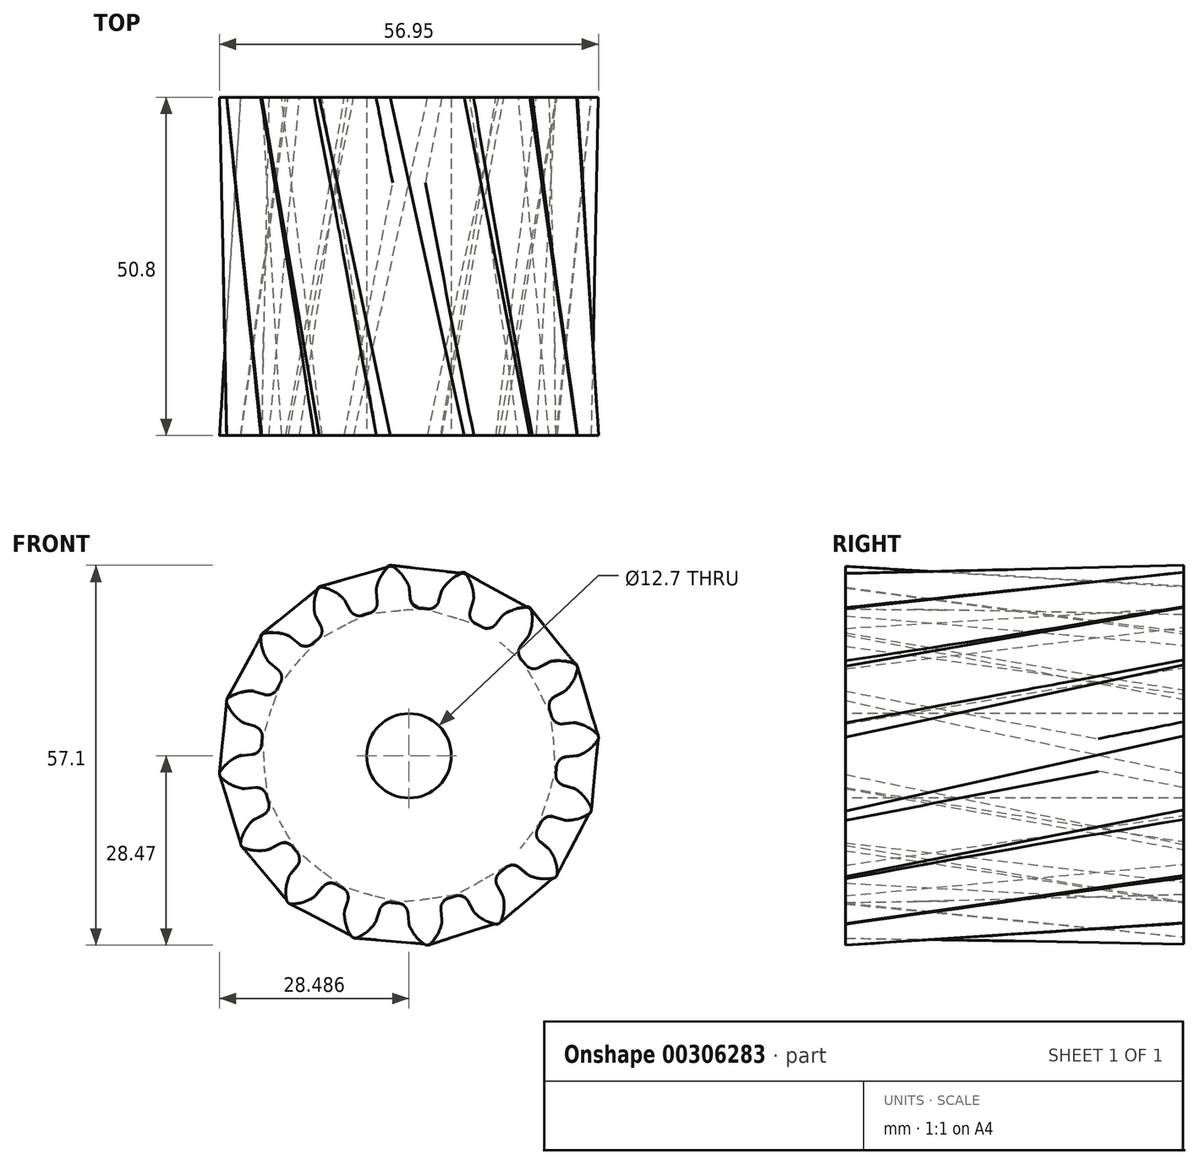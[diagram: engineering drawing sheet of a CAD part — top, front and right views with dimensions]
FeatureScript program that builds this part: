
annotation { "Feature Type Name" : "Feature", "Feature Type Description" : "" }
export const myFeature = defineFeature(function(context is Context, id is Id, definition is map)
    precondition{}
    {
        {
            var Q0;
            Q0=qCreatedBy(makeId("Front.planeOp"),FACE);
            var sketch = newSketch(context, id + "F0", { "sketchPlane" : qUnion([Q0])});
            skArc(sketch, "E0", {"start": v(-5.93, 21.42) * mm, "mid": v(-6.45, 21.27) * mm, "end": v(-6.97, 21.1) * mm});
            skArc(sketch, "E1.trimOffspring", {"start": v(-0.1, 25.65) * mm, "mid": v(-1.04, 27.17) * mm, "end": v(-2.37, 28.38) * mm});
            skLineSegment(sketch, "E2", {"start": v(0.02, 25.17) * mm, "end": v(0.18, 23.6) * mm});
            skLineSegment(sketch, "E3", {"start": v(-2.65, 28.47) * mm, "end": v(-2.8, 28.47) * mm});
            skLineSegment(sketch, "E4.MirrorCS", {"start": v(-2.95, 28.44) * mm, "end": v(-2.8, 28.47) * mm});
            skArc(sketch, "E5.MirrorCS", {"start": v(-4.9, 25.17) * mm, "mid": v(-4.28, 26.85) * mm, "end": v(-3.22, 28.3) * mm});
            skLineSegment(sketch, "E6.MirrorCS", {"start": v(-4.93, 24.68) * mm, "end": v(-4.78, 23.1) * mm});
            skPoint(sketch, "E7.visualSharp", {"position": v(0.31, 22.22) * mm});
            skArc(sketch, "E7.filletArc", {"start": v(0.18, 23.6) * mm, "mid": v(0.65, 22.61) * mm, "end": v(1.64, 22.16) * mm});
            skPoint(sketch, "E8.visualSharp", {"position": v(-4.64, 21.73) * mm});
            skArc(sketch, "E8.filletArc", {"start": v(-5.93, 21.42) * mm, "mid": v(-5.05, 22.05) * mm, "end": v(-4.78, 23.1) * mm});
            skPoint(sketch, "E9.visualSharp", {"position": v(-4.96, 24.91) * mm});
            skArc(sketch, "E9.filletArc", {"start": v(-4.9, 25.17) * mm, "mid": v(-4.94, 24.93) * mm, "end": v(-4.93, 24.68) * mm});
            skPoint(sketch, "E10.visualSharp", {"position": v(0, 25.4) * mm});
            skArc(sketch, "E10.filletArc", {"start": v(0.02, 25.17) * mm, "mid": v(-0.02, 25.41) * mm, "end": v(-0.1, 25.65) * mm});
            skPoint(sketch, "E11.visualSharp", {"position": v(-3.1, 28.4) * mm});
            skArc(sketch, "E11.filletArc", {"start": v(-2.95, 28.44) * mm, "mid": v(-3.1, 28.38) * mm, "end": v(-3.22, 28.3) * mm});
            skPoint(sketch, "E12.visualSharp", {"position": v(-2.5, 28.47) * mm});
            skArc(sketch, "E12.filletArc", {"start": v(-2.37, 28.38) * mm, "mid": v(-2.5, 28.44) * mm, "end": v(-2.65, 28.47) * mm});
            skArc(sketch, "E13.1.0", {"start": v(-13.68, 17.52) * mm, "mid": v(-13.1, 18.44) * mm, "end": v(-13.26, 19.52) * mm});
            skPoint(sketch, "E13.1.1", {"position": v(-14.11, 21.12) * mm});
            skLineSegment(sketch, "E13.1.2", {"start": v(-9.61, 23.26) * mm, "end": v(-8.86, 21.86) * mm});
            skPoint(sketch, "E13.1.3", {"position": v(-9.72, 23.47) * mm});
            skArc(sketch, "E13.1.4", {"start": v(-14.16, 21.38) * mm, "mid": v(-14.23, 23.17) * mm, "end": v(-13.8, 24.9) * mm});
            skLineSegment(sketch, "E13.1.5", {"start": v(-14, 20.92) * mm, "end": v(-13.26, 19.52) * mm});
            skArc(sketch, "E13.1.6", {"start": v(-8.86, 21.86) * mm, "mid": v(-8.05, 21.14) * mm, "end": v(-6.97, 21.1) * mm});
            skArc(sketch, "E13.1.7", {"start": v(-9.9, 23.66) * mm, "mid": v(-11.36, 24.7) * mm, "end": v(-13.05, 25.31) * mm});
            skPoint(sketch, "E13.1.8", {"position": v(-13.74, 25.06) * mm});
            skPoint(sketch, "E13.1.9", {"position": v(-13.2, 25.34) * mm});
            skArc(sketch, "E13.1.10", {"start": v(-14.16, 21.38) * mm, "mid": v(-14.1, 21.14) * mm, "end": v(-14, 20.92) * mm});
            skArc(sketch, "E13.1.11", {"start": v(-9.61, 23.26) * mm, "mid": v(-9.74, 23.47) * mm, "end": v(-9.9, 23.66) * mm});
            skLineSegment(sketch, "E13.1.12", {"start": v(-13.34, 25.28) * mm, "end": v(-13.48, 25.23) * mm});
            skLineSegment(sketch, "E13.1.13", {"start": v(-13.61, 25.14) * mm, "end": v(-13.48, 25.23) * mm});
            skArc(sketch, "E13.1.14", {"start": v(-13.61, 25.14) * mm, "mid": v(-13.72, 25.04) * mm, "end": v(-13.8, 24.9) * mm});
            skArc(sketch, "E13.1.15", {"start": v(-13.05, 25.31) * mm, "mid": v(-13.2, 25.32) * mm, "end": v(-13.34, 25.28) * mm});
            skArc(sketch, "E13.2.0", {"start": v(-19.34, 10.95) * mm, "mid": v(-19.16, 12.02) * mm, "end": v(-19.71, 12.96) * mm});
            skPoint(sketch, "E13.2.1", {"position": v(-21.12, 14.11) * mm});
            skLineSegment(sketch, "E13.2.2", {"start": v(-17.78, 17.81) * mm, "end": v(-16.56, 16.8) * mm});
            skPoint(sketch, "E13.2.3", {"position": v(-17.96, 17.96) * mm});
            skArc(sketch, "E13.2.4", {"start": v(-21.27, 14.33) * mm, "mid": v(-22.02, 15.96) * mm, "end": v(-22.28, 17.73) * mm});
            skLineSegment(sketch, "E13.2.5", {"start": v(-20.94, 13.97) * mm, "end": v(-19.71, 12.96) * mm});
            skArc(sketch, "E13.2.6", {"start": v(-16.56, 16.8) * mm, "mid": v(-15.53, 16.45) * mm, "end": v(-14.51, 16.83) * mm});
            skArc(sketch, "E13.2.7", {"start": v(-18.2, 18.06) * mm, "mid": v(-19.95, 18.48) * mm, "end": v(-21.74, 18.4) * mm});
            skPoint(sketch, "E13.2.8", {"position": v(-22.28, 17.9) * mm});
            skPoint(sketch, "E13.2.9", {"position": v(-21.9, 18.36) * mm});
            skArc(sketch, "E13.2.10", {"start": v(-21.27, 14.33) * mm, "mid": v(-21.12, 14.14) * mm, "end": v(-20.94, 13.97) * mm});
            skArc(sketch, "E13.2.11", {"start": v(-17.78, 17.81) * mm, "mid": v(-17.98, 17.96) * mm, "end": v(-18.2, 18.06) * mm});
            skLineSegment(sketch, "E13.2.12", {"start": v(-22, 18.25) * mm, "end": v(-22.11, 18.15) * mm});
            skLineSegment(sketch, "E13.2.13", {"start": v(-22.2, 18.02) * mm, "end": v(-22.11, 18.15) * mm});
            skArc(sketch, "E13.2.14", {"start": v(-22.2, 18.02) * mm, "mid": v(-22.26, 17.88) * mm, "end": v(-22.28, 17.73) * mm});
            skArc(sketch, "E13.2.15", {"start": v(-21.74, 18.4) * mm, "mid": v(-21.88, 18.34) * mm, "end": v(-22, 18.25) * mm});
            skArc(sketch, "E13.3.0", {"start": v(-22.06, 2.71) * mm, "mid": v(-22.3, 3.77) * mm, "end": v(-23.17, 4.43) * mm});
            skPoint(sketch, "E13.3.1", {"position": v(-24.91, 4.96) * mm});
            skLineSegment(sketch, "E13.3.2", {"start": v(-23.25, 9.65) * mm, "end": v(-21.73, 9.2) * mm});
            skPoint(sketch, "E13.3.3", {"position": v(-23.47, 9.72) * mm});
            skArc(sketch, "E13.3.4", {"start": v(-25.13, 5.1) * mm, "mid": v(-26.45, 6.32) * mm, "end": v(-27.37, 7.86) * mm});
            skLineSegment(sketch, "E13.3.5", {"start": v(-24.7, 4.89) * mm, "end": v(-23.17, 4.43) * mm});
            skArc(sketch, "E13.3.6", {"start": v(-21.73, 9.2) * mm, "mid": v(-20.64, 9.25) * mm, "end": v(-19.85, 10) * mm});
            skArc(sketch, "E13.3.7", {"start": v(-23.73, 9.72) * mm, "mid": v(-25.5, 9.44) * mm, "end": v(-27.12, 8.67) * mm});
            skPoint(sketch, "E13.3.8", {"position": v(-27.43, 8) * mm});
            skPoint(sketch, "E13.3.9", {"position": v(-27.25, 8.59) * mm});
            skArc(sketch, "E13.3.10", {"start": v(-25.13, 5.1) * mm, "mid": v(-24.92, 4.98) * mm, "end": v(-24.7, 4.89) * mm});
            skArc(sketch, "E13.3.11", {"start": v(-23.25, 9.65) * mm, "mid": v(-23.49, 9.7) * mm, "end": v(-23.73, 9.72) * mm});
            skLineSegment(sketch, "E13.3.12", {"start": v(-27.31, 8.44) * mm, "end": v(-27.37, 8.3) * mm});
            skLineSegment(sketch, "E13.3.13", {"start": v(-27.4, 8.15) * mm, "end": v(-27.37, 8.3) * mm});
            skArc(sketch, "E13.3.14", {"start": v(-27.4, 8.15) * mm, "mid": v(-27.4, 8) * mm, "end": v(-27.37, 7.86) * mm});
            skArc(sketch, "E13.3.15", {"start": v(-27.12, 8.67) * mm, "mid": v(-27.24, 8.57) * mm, "end": v(-27.31, 8.44) * mm});
            skArc(sketch, "E13.4.0", {"start": v(-21.42, -5.93) * mm, "mid": v(-22.05, -5.05) * mm, "end": v(-23.1, -4.78) * mm});
            skPoint(sketch, "E13.4.1", {"position": v(-24.91, -4.96) * mm});
            skLineSegment(sketch, "E13.4.2", {"start": v(-25.17, 0.02) * mm, "end": v(-23.6, 0.18) * mm});
            skPoint(sketch, "E13.4.3", {"position": v(-25.4, 0) * mm});
            skArc(sketch, "E13.4.4", {"start": v(-25.17, -4.9) * mm, "mid": v(-26.85, -4.28) * mm, "end": v(-28.3, -3.22) * mm});
            skLineSegment(sketch, "E13.4.5", {"start": v(-24.68, -4.93) * mm, "end": v(-23.1, -4.78) * mm});
            skArc(sketch, "E13.4.6", {"start": v(-23.6, 0.18) * mm, "mid": v(-22.61, 0.65) * mm, "end": v(-22.16, 1.64) * mm});
            skArc(sketch, "E13.4.7", {"start": v(-25.65, -0.1) * mm, "mid": v(-27.17, -1.04) * mm, "end": v(-28.38, -2.37) * mm});
            skPoint(sketch, "E13.4.8", {"position": v(-28.4, -3.1) * mm});
            skPoint(sketch, "E13.4.9", {"position": v(-28.47, -2.5) * mm});
            skArc(sketch, "E13.4.10", {"start": v(-25.17, -4.9) * mm, "mid": v(-24.93, -4.94) * mm, "end": v(-24.68, -4.93) * mm});
            skArc(sketch, "E13.4.11", {"start": v(-25.17, 0.02) * mm, "mid": v(-25.41, -0.02) * mm, "end": v(-25.65, -0.1) * mm});
            skLineSegment(sketch, "E13.4.12", {"start": v(-28.47, -2.65) * mm, "end": v(-28.47, -2.8) * mm});
            skLineSegment(sketch, "E13.4.13", {"start": v(-28.44, -2.95) * mm, "end": v(-28.47, -2.8) * mm});
            skArc(sketch, "E13.4.14", {"start": v(-28.44, -2.95) * mm, "mid": v(-28.38, -3.1) * mm, "end": v(-28.3, -3.22) * mm});
            skArc(sketch, "E13.4.15", {"start": v(-28.38, -2.37) * mm, "mid": v(-28.44, -2.5) * mm, "end": v(-28.47, -2.65) * mm});
            skArc(sketch, "E13.5.0", {"start": v(-17.52, -13.68) * mm, "mid": v(-18.44, -13.1) * mm, "end": v(-19.52, -13.26) * mm});
            skPoint(sketch, "E13.5.1", {"position": v(-21.12, -14.11) * mm});
            skLineSegment(sketch, "E13.5.2", {"start": v(-23.26, -9.61) * mm, "end": v(-21.86, -8.86) * mm});
            skPoint(sketch, "E13.5.3", {"position": v(-23.47, -9.72) * mm});
            skArc(sketch, "E13.5.4", {"start": v(-21.38, -14.16) * mm, "mid": v(-23.17, -14.23) * mm, "end": v(-24.9, -13.8) * mm});
            skLineSegment(sketch, "E13.5.5", {"start": v(-20.92, -14) * mm, "end": v(-19.52, -13.26) * mm});
            skArc(sketch, "E13.5.6", {"start": v(-21.86, -8.86) * mm, "mid": v(-21.14, -8.05) * mm, "end": v(-21.1, -6.97) * mm});
            skArc(sketch, "E13.5.7", {"start": v(-23.66, -9.9) * mm, "mid": v(-24.7, -11.36) * mm, "end": v(-25.31, -13.05) * mm});
            skPoint(sketch, "E13.5.8", {"position": v(-25.06, -13.74) * mm});
            skPoint(sketch, "E13.5.9", {"position": v(-25.34, -13.2) * mm});
            skArc(sketch, "E13.5.10", {"start": v(-21.38, -14.16) * mm, "mid": v(-21.14, -14.1) * mm, "end": v(-20.92, -14) * mm});
            skArc(sketch, "E13.5.11", {"start": v(-23.26, -9.61) * mm, "mid": v(-23.47, -9.74) * mm, "end": v(-23.66, -9.9) * mm});
            skLineSegment(sketch, "E13.5.12", {"start": v(-25.28, -13.34) * mm, "end": v(-25.23, -13.48) * mm});
            skLineSegment(sketch, "E13.5.13", {"start": v(-25.14, -13.61) * mm, "end": v(-25.23, -13.48) * mm});
            skArc(sketch, "E13.5.14", {"start": v(-25.14, -13.61) * mm, "mid": v(-25.04, -13.72) * mm, "end": v(-24.9, -13.8) * mm});
            skArc(sketch, "E13.5.15", {"start": v(-25.31, -13.05) * mm, "mid": v(-25.32, -13.2) * mm, "end": v(-25.28, -13.34) * mm});
            skArc(sketch, "E13.6.0", {"start": v(-10.95, -19.34) * mm, "mid": v(-12.02, -19.16) * mm, "end": v(-12.96, -19.71) * mm});
            skPoint(sketch, "E13.6.1", {"position": v(-14.11, -21.12) * mm});
            skLineSegment(sketch, "E13.6.2", {"start": v(-17.81, -17.78) * mm, "end": v(-16.8, -16.56) * mm});
            skPoint(sketch, "E13.6.3", {"position": v(-17.96, -17.96) * mm});
            skArc(sketch, "E13.6.4", {"start": v(-14.33, -21.27) * mm, "mid": v(-15.96, -22.02) * mm, "end": v(-17.73, -22.28) * mm});
            skLineSegment(sketch, "E13.6.5", {"start": v(-13.97, -20.94) * mm, "end": v(-12.96, -19.71) * mm});
            skArc(sketch, "E13.6.6", {"start": v(-16.8, -16.56) * mm, "mid": v(-16.45, -15.53) * mm, "end": v(-16.83, -14.51) * mm});
            skArc(sketch, "E13.6.7", {"start": v(-18.06, -18.2) * mm, "mid": v(-18.48, -19.95) * mm, "end": v(-18.4, -21.74) * mm});
            skPoint(sketch, "E13.6.8", {"position": v(-17.9, -22.28) * mm});
            skPoint(sketch, "E13.6.9", {"position": v(-18.36, -21.9) * mm});
            skArc(sketch, "E13.6.10", {"start": v(-14.33, -21.27) * mm, "mid": v(-14.14, -21.12) * mm, "end": v(-13.97, -20.94) * mm});
            skArc(sketch, "E13.6.11", {"start": v(-17.81, -17.78) * mm, "mid": v(-17.96, -17.98) * mm, "end": v(-18.06, -18.2) * mm});
            skLineSegment(sketch, "E13.6.12", {"start": v(-18.25, -22) * mm, "end": v(-18.15, -22.11) * mm});
            skLineSegment(sketch, "E13.6.13", {"start": v(-18.02, -22.2) * mm, "end": v(-18.15, -22.11) * mm});
            skArc(sketch, "E13.6.14", {"start": v(-18.02, -22.2) * mm, "mid": v(-17.88, -22.26) * mm, "end": v(-17.73, -22.28) * mm});
            skArc(sketch, "E13.6.15", {"start": v(-18.4, -21.74) * mm, "mid": v(-18.34, -21.88) * mm, "end": v(-18.25, -22) * mm});
            skArc(sketch, "E13.7.0", {"start": v(-2.71, -22.06) * mm, "mid": v(-3.77, -22.3) * mm, "end": v(-4.43, -23.17) * mm});
            skPoint(sketch, "E13.7.1", {"position": v(-4.96, -24.91) * mm});
            skLineSegment(sketch, "E13.7.2", {"start": v(-9.65, -23.25) * mm, "end": v(-9.2, -21.73) * mm});
            skPoint(sketch, "E13.7.3", {"position": v(-9.72, -23.47) * mm});
            skArc(sketch, "E13.7.4", {"start": v(-5.1, -25.13) * mm, "mid": v(-6.32, -26.45) * mm, "end": v(-7.86, -27.37) * mm});
            skLineSegment(sketch, "E13.7.5", {"start": v(-4.89, -24.7) * mm, "end": v(-4.43, -23.17) * mm});
            skArc(sketch, "E13.7.6", {"start": v(-9.2, -21.73) * mm, "mid": v(-9.25, -20.64) * mm, "end": v(-10, -19.85) * mm});
            skArc(sketch, "E13.7.7", {"start": v(-9.72, -23.73) * mm, "mid": v(-9.44, -25.5) * mm, "end": v(-8.67, -27.12) * mm});
            skPoint(sketch, "E13.7.8", {"position": v(-8, -27.43) * mm});
            skPoint(sketch, "E13.7.9", {"position": v(-8.59, -27.25) * mm});
            skArc(sketch, "E13.7.10", {"start": v(-5.1, -25.13) * mm, "mid": v(-4.98, -24.92) * mm, "end": v(-4.89, -24.7) * mm});
            skArc(sketch, "E13.7.11", {"start": v(-9.65, -23.25) * mm, "mid": v(-9.7, -23.49) * mm, "end": v(-9.72, -23.73) * mm});
            skLineSegment(sketch, "E13.7.12", {"start": v(-8.44, -27.31) * mm, "end": v(-8.3, -27.37) * mm});
            skLineSegment(sketch, "E13.7.13", {"start": v(-8.15, -27.4) * mm, "end": v(-8.3, -27.37) * mm});
            skArc(sketch, "E13.7.14", {"start": v(-8.15, -27.4) * mm, "mid": v(-8, -27.4) * mm, "end": v(-7.86, -27.37) * mm});
            skArc(sketch, "E13.7.15", {"start": v(-8.67, -27.12) * mm, "mid": v(-8.57, -27.24) * mm, "end": v(-8.44, -27.31) * mm});
            skArc(sketch, "E13.8.0", {"start": v(5.93, -21.42) * mm, "mid": v(5.05, -22.05) * mm, "end": v(4.78, -23.1) * mm});
            skPoint(sketch, "E13.8.1", {"position": v(4.96, -24.91) * mm});
            skLineSegment(sketch, "E13.8.2", {"start": v(-0.02, -25.17) * mm, "end": v(-0.18, -23.6) * mm});
            skPoint(sketch, "E13.8.3", {"position": v(0, -25.4) * mm});
            skArc(sketch, "E13.8.4", {"start": v(4.9, -25.17) * mm, "mid": v(4.28, -26.85) * mm, "end": v(3.22, -28.3) * mm});
            skLineSegment(sketch, "E13.8.5", {"start": v(4.93, -24.68) * mm, "end": v(4.78, -23.1) * mm});
            skArc(sketch, "E13.8.6", {"start": v(-0.18, -23.6) * mm, "mid": v(-0.65, -22.61) * mm, "end": v(-1.64, -22.16) * mm});
            skArc(sketch, "E13.8.7", {"start": v(0.1, -25.65) * mm, "mid": v(1.04, -27.17) * mm, "end": v(2.37, -28.38) * mm});
            skPoint(sketch, "E13.8.8", {"position": v(3.1, -28.4) * mm});
            skPoint(sketch, "E13.8.9", {"position": v(2.5, -28.47) * mm});
            skArc(sketch, "E13.8.10", {"start": v(4.9, -25.17) * mm, "mid": v(4.94, -24.93) * mm, "end": v(4.93, -24.68) * mm});
            skArc(sketch, "E13.8.11", {"start": v(-0.02, -25.17) * mm, "mid": v(0.02, -25.41) * mm, "end": v(0.1, -25.65) * mm});
            skLineSegment(sketch, "E13.8.12", {"start": v(2.65, -28.47) * mm, "end": v(2.8, -28.47) * mm});
            skLineSegment(sketch, "E13.8.13", {"start": v(2.95, -28.44) * mm, "end": v(2.8, -28.47) * mm});
            skArc(sketch, "E13.8.14", {"start": v(2.95, -28.44) * mm, "mid": v(3.1, -28.38) * mm, "end": v(3.22, -28.3) * mm});
            skArc(sketch, "E13.8.15", {"start": v(2.37, -28.38) * mm, "mid": v(2.5, -28.44) * mm, "end": v(2.65, -28.47) * mm});
            skArc(sketch, "E13.9.0", {"start": v(13.68, -17.52) * mm, "mid": v(13.1, -18.44) * mm, "end": v(13.26, -19.52) * mm});
            skPoint(sketch, "E13.9.1", {"position": v(14.11, -21.12) * mm});
            skLineSegment(sketch, "E13.9.2", {"start": v(9.61, -23.26) * mm, "end": v(8.86, -21.86) * mm});
            skPoint(sketch, "E13.9.3", {"position": v(9.72, -23.47) * mm});
            skArc(sketch, "E13.9.4", {"start": v(14.16, -21.38) * mm, "mid": v(14.23, -23.17) * mm, "end": v(13.8, -24.9) * mm});
            skLineSegment(sketch, "E13.9.5", {"start": v(14, -20.92) * mm, "end": v(13.26, -19.52) * mm});
            skArc(sketch, "E13.9.6", {"start": v(8.86, -21.86) * mm, "mid": v(8.05, -21.14) * mm, "end": v(6.97, -21.1) * mm});
            skArc(sketch, "E13.9.7", {"start": v(9.9, -23.66) * mm, "mid": v(11.36, -24.7) * mm, "end": v(13.05, -25.31) * mm});
            skPoint(sketch, "E13.9.8", {"position": v(13.74, -25.06) * mm});
            skPoint(sketch, "E13.9.9", {"position": v(13.2, -25.34) * mm});
            skArc(sketch, "E13.9.10", {"start": v(14.16, -21.38) * mm, "mid": v(14.1, -21.14) * mm, "end": v(14, -20.92) * mm});
            skArc(sketch, "E13.9.11", {"start": v(9.61, -23.26) * mm, "mid": v(9.74, -23.47) * mm, "end": v(9.9, -23.66) * mm});
            skLineSegment(sketch, "E13.9.12", {"start": v(13.34, -25.28) * mm, "end": v(13.48, -25.23) * mm});
            skLineSegment(sketch, "E13.9.13", {"start": v(13.61, -25.14) * mm, "end": v(13.48, -25.23) * mm});
            skArc(sketch, "E13.9.14", {"start": v(13.61, -25.14) * mm, "mid": v(13.72, -25.04) * mm, "end": v(13.8, -24.9) * mm});
            skArc(sketch, "E13.9.15", {"start": v(13.05, -25.31) * mm, "mid": v(13.2, -25.32) * mm, "end": v(13.34, -25.28) * mm});
            skArc(sketch, "E13.10.0", {"start": v(19.34, -10.95) * mm, "mid": v(19.16, -12.02) * mm, "end": v(19.71, -12.96) * mm});
            skPoint(sketch, "E13.10.1", {"position": v(21.12, -14.11) * mm});
            skLineSegment(sketch, "E13.10.2", {"start": v(17.78, -17.81) * mm, "end": v(16.56, -16.8) * mm});
            skPoint(sketch, "E13.10.3", {"position": v(17.96, -17.96) * mm});
            skArc(sketch, "E13.10.4", {"start": v(21.27, -14.33) * mm, "mid": v(22.02, -15.96) * mm, "end": v(22.28, -17.73) * mm});
            skLineSegment(sketch, "E13.10.5", {"start": v(20.94, -13.97) * mm, "end": v(19.71, -12.96) * mm});
            skArc(sketch, "E13.10.6", {"start": v(16.56, -16.8) * mm, "mid": v(15.53, -16.45) * mm, "end": v(14.51, -16.83) * mm});
            skArc(sketch, "E13.10.7", {"start": v(18.2, -18.06) * mm, "mid": v(19.95, -18.48) * mm, "end": v(21.74, -18.4) * mm});
            skPoint(sketch, "E13.10.8", {"position": v(22.28, -17.9) * mm});
            skPoint(sketch, "E13.10.9", {"position": v(21.9, -18.36) * mm});
            skArc(sketch, "E13.10.10", {"start": v(21.27, -14.33) * mm, "mid": v(21.12, -14.14) * mm, "end": v(20.94, -13.97) * mm});
            skArc(sketch, "E13.10.11", {"start": v(17.78, -17.81) * mm, "mid": v(17.98, -17.96) * mm, "end": v(18.2, -18.06) * mm});
            skLineSegment(sketch, "E13.10.12", {"start": v(22, -18.25) * mm, "end": v(22.11, -18.15) * mm});
            skLineSegment(sketch, "E13.10.13", {"start": v(22.2, -18.02) * mm, "end": v(22.11, -18.15) * mm});
            skArc(sketch, "E13.10.14", {"start": v(22.2, -18.02) * mm, "mid": v(22.26, -17.88) * mm, "end": v(22.28, -17.73) * mm});
            skArc(sketch, "E13.10.15", {"start": v(21.74, -18.4) * mm, "mid": v(21.88, -18.34) * mm, "end": v(22, -18.25) * mm});
            skArc(sketch, "E13.11.0", {"start": v(22.06, -2.71) * mm, "mid": v(22.3, -3.77) * mm, "end": v(23.17, -4.43) * mm});
            skPoint(sketch, "E13.11.1", {"position": v(24.91, -4.96) * mm});
            skLineSegment(sketch, "E13.11.2", {"start": v(23.25, -9.65) * mm, "end": v(21.73, -9.2) * mm});
            skPoint(sketch, "E13.11.3", {"position": v(23.47, -9.72) * mm});
            skArc(sketch, "E13.11.4", {"start": v(25.13, -5.1) * mm, "mid": v(26.45, -6.32) * mm, "end": v(27.37, -7.86) * mm});
            skLineSegment(sketch, "E13.11.5", {"start": v(24.7, -4.89) * mm, "end": v(23.17, -4.43) * mm});
            skArc(sketch, "E13.11.6", {"start": v(21.73, -9.2) * mm, "mid": v(20.64, -9.25) * mm, "end": v(19.85, -10) * mm});
            skArc(sketch, "E13.11.7", {"start": v(23.73, -9.72) * mm, "mid": v(25.5, -9.44) * mm, "end": v(27.12, -8.67) * mm});
            skPoint(sketch, "E13.11.8", {"position": v(27.43, -8) * mm});
            skPoint(sketch, "E13.11.9", {"position": v(27.25, -8.59) * mm});
            skArc(sketch, "E13.11.10", {"start": v(25.13, -5.1) * mm, "mid": v(24.92, -4.98) * mm, "end": v(24.7, -4.89) * mm});
            skArc(sketch, "E13.11.11", {"start": v(23.25, -9.65) * mm, "mid": v(23.49, -9.7) * mm, "end": v(23.73, -9.72) * mm});
            skLineSegment(sketch, "E13.11.12", {"start": v(27.31, -8.44) * mm, "end": v(27.37, -8.3) * mm});
            skLineSegment(sketch, "E13.11.13", {"start": v(27.4, -8.15) * mm, "end": v(27.37, -8.3) * mm});
            skArc(sketch, "E13.11.14", {"start": v(27.4, -8.15) * mm, "mid": v(27.4, -8) * mm, "end": v(27.37, -7.86) * mm});
            skArc(sketch, "E13.11.15", {"start": v(27.12, -8.67) * mm, "mid": v(27.24, -8.57) * mm, "end": v(27.31, -8.44) * mm});
            skArc(sketch, "E13.12.0", {"start": v(21.42, 5.93) * mm, "mid": v(22.05, 5.05) * mm, "end": v(23.1, 4.78) * mm});
            skPoint(sketch, "E13.12.1", {"position": v(24.91, 4.96) * mm});
            skLineSegment(sketch, "E13.12.2", {"start": v(25.17, -0.02) * mm, "end": v(23.6, -0.18) * mm});
            skPoint(sketch, "E13.12.3", {"position": v(25.4, 0) * mm});
            skArc(sketch, "E13.12.4", {"start": v(25.17, 4.9) * mm, "mid": v(26.85, 4.28) * mm, "end": v(28.3, 3.22) * mm});
            skLineSegment(sketch, "E13.12.5", {"start": v(24.68, 4.93) * mm, "end": v(23.1, 4.78) * mm});
            skArc(sketch, "E13.12.6", {"start": v(23.6, -0.18) * mm, "mid": v(22.61, -0.65) * mm, "end": v(22.16, -1.64) * mm});
            skArc(sketch, "E13.12.7", {"start": v(25.65, 0.1) * mm, "mid": v(27.17, 1.04) * mm, "end": v(28.38, 2.37) * mm});
            skPoint(sketch, "E13.12.8", {"position": v(28.4, 3.1) * mm});
            skPoint(sketch, "E13.12.9", {"position": v(28.47, 2.5) * mm});
            skArc(sketch, "E13.12.10", {"start": v(25.17, 4.9) * mm, "mid": v(24.93, 4.94) * mm, "end": v(24.68, 4.93) * mm});
            skArc(sketch, "E13.12.11", {"start": v(25.17, -0.02) * mm, "mid": v(25.41, 0.02) * mm, "end": v(25.65, 0.1) * mm});
            skLineSegment(sketch, "E13.12.12", {"start": v(28.47, 2.65) * mm, "end": v(28.47, 2.8) * mm});
            skLineSegment(sketch, "E13.12.13", {"start": v(28.44, 2.95) * mm, "end": v(28.47, 2.8) * mm});
            skArc(sketch, "E13.12.14", {"start": v(28.44, 2.95) * mm, "mid": v(28.38, 3.1) * mm, "end": v(28.3, 3.22) * mm});
            skArc(sketch, "E13.12.15", {"start": v(28.38, 2.37) * mm, "mid": v(28.44, 2.5) * mm, "end": v(28.47, 2.65) * mm});
            skArc(sketch, "E13.13.0", {"start": v(17.52, 13.68) * mm, "mid": v(18.44, 13.1) * mm, "end": v(19.52, 13.26) * mm});
            skPoint(sketch, "E13.13.1", {"position": v(21.12, 14.11) * mm});
            skLineSegment(sketch, "E13.13.2", {"start": v(23.26, 9.61) * mm, "end": v(21.86, 8.86) * mm});
            skPoint(sketch, "E13.13.3", {"position": v(23.47, 9.72) * mm});
            skArc(sketch, "E13.13.4", {"start": v(21.38, 14.16) * mm, "mid": v(23.17, 14.23) * mm, "end": v(24.9, 13.8) * mm});
            skLineSegment(sketch, "E13.13.5", {"start": v(20.92, 14) * mm, "end": v(19.52, 13.26) * mm});
            skArc(sketch, "E13.13.6", {"start": v(21.86, 8.86) * mm, "mid": v(21.14, 8.05) * mm, "end": v(21.1, 6.97) * mm});
            skArc(sketch, "E13.13.7", {"start": v(23.66, 9.9) * mm, "mid": v(24.7, 11.36) * mm, "end": v(25.31, 13.05) * mm});
            skPoint(sketch, "E13.13.8", {"position": v(25.06, 13.74) * mm});
            skPoint(sketch, "E13.13.9", {"position": v(25.34, 13.2) * mm});
            skArc(sketch, "E13.13.10", {"start": v(21.38, 14.16) * mm, "mid": v(21.14, 14.1) * mm, "end": v(20.92, 14) * mm});
            skArc(sketch, "E13.13.11", {"start": v(23.26, 9.61) * mm, "mid": v(23.47, 9.74) * mm, "end": v(23.66, 9.9) * mm});
            skLineSegment(sketch, "E13.13.12", {"start": v(25.28, 13.34) * mm, "end": v(25.23, 13.48) * mm});
            skLineSegment(sketch, "E13.13.13", {"start": v(25.14, 13.61) * mm, "end": v(25.23, 13.48) * mm});
            skArc(sketch, "E13.13.14", {"start": v(25.14, 13.61) * mm, "mid": v(25.04, 13.72) * mm, "end": v(24.9, 13.8) * mm});
            skArc(sketch, "E13.13.15", {"start": v(25.31, 13.05) * mm, "mid": v(25.32, 13.2) * mm, "end": v(25.28, 13.34) * mm});
            skArc(sketch, "E13.14.0", {"start": v(10.95, 19.34) * mm, "mid": v(12.02, 19.16) * mm, "end": v(12.96, 19.71) * mm});
            skPoint(sketch, "E13.14.1", {"position": v(14.11, 21.12) * mm});
            skLineSegment(sketch, "E13.14.2", {"start": v(17.81, 17.78) * mm, "end": v(16.8, 16.56) * mm});
            skPoint(sketch, "E13.14.3", {"position": v(17.96, 17.96) * mm});
            skArc(sketch, "E13.14.4", {"start": v(14.33, 21.27) * mm, "mid": v(15.96, 22.02) * mm, "end": v(17.73, 22.28) * mm});
            skLineSegment(sketch, "E13.14.5", {"start": v(13.97, 20.94) * mm, "end": v(12.96, 19.71) * mm});
            skArc(sketch, "E13.14.6", {"start": v(16.8, 16.56) * mm, "mid": v(16.45, 15.53) * mm, "end": v(16.83, 14.51) * mm});
            skArc(sketch, "E13.14.7", {"start": v(18.06, 18.2) * mm, "mid": v(18.48, 19.95) * mm, "end": v(18.4, 21.74) * mm});
            skPoint(sketch, "E13.14.8", {"position": v(17.9, 22.28) * mm});
            skPoint(sketch, "E13.14.9", {"position": v(18.36, 21.9) * mm});
            skArc(sketch, "E13.14.10", {"start": v(14.33, 21.27) * mm, "mid": v(14.14, 21.12) * mm, "end": v(13.97, 20.94) * mm});
            skArc(sketch, "E13.14.11", {"start": v(17.81, 17.78) * mm, "mid": v(17.96, 17.98) * mm, "end": v(18.06, 18.2) * mm});
            skLineSegment(sketch, "E13.14.12", {"start": v(18.25, 22) * mm, "end": v(18.15, 22.11) * mm});
            skLineSegment(sketch, "E13.14.13", {"start": v(18.02, 22.2) * mm, "end": v(18.15, 22.11) * mm});
            skArc(sketch, "E13.14.14", {"start": v(18.02, 22.2) * mm, "mid": v(17.88, 22.26) * mm, "end": v(17.73, 22.28) * mm});
            skArc(sketch, "E13.14.15", {"start": v(18.4, 21.74) * mm, "mid": v(18.34, 21.88) * mm, "end": v(18.25, 22) * mm});
            skArc(sketch, "E13.15.0", {"start": v(2.71, 22.06) * mm, "mid": v(3.77, 22.3) * mm, "end": v(4.43, 23.17) * mm});
            skPoint(sketch, "E13.15.1", {"position": v(4.96, 24.91) * mm});
            skLineSegment(sketch, "E13.15.2", {"start": v(9.65, 23.25) * mm, "end": v(9.2, 21.73) * mm});
            skPoint(sketch, "E13.15.3", {"position": v(9.72, 23.47) * mm});
            skArc(sketch, "E13.15.4", {"start": v(5.1, 25.13) * mm, "mid": v(6.32, 26.45) * mm, "end": v(7.86, 27.37) * mm});
            skLineSegment(sketch, "E13.15.5", {"start": v(4.89, 24.7) * mm, "end": v(4.43, 23.17) * mm});
            skArc(sketch, "E13.15.6", {"start": v(9.2, 21.73) * mm, "mid": v(9.25, 20.64) * mm, "end": v(10, 19.85) * mm});
            skArc(sketch, "E13.15.7", {"start": v(9.72, 23.73) * mm, "mid": v(9.44, 25.5) * mm, "end": v(8.67, 27.12) * mm});
            skPoint(sketch, "E13.15.8", {"position": v(8, 27.43) * mm});
            skPoint(sketch, "E13.15.9", {"position": v(8.59, 27.25) * mm});
            skArc(sketch, "E13.15.10", {"start": v(5.1, 25.13) * mm, "mid": v(4.98, 24.92) * mm, "end": v(4.89, 24.7) * mm});
            skArc(sketch, "E13.15.11", {"start": v(9.65, 23.25) * mm, "mid": v(9.7, 23.49) * mm, "end": v(9.72, 23.73) * mm});
            skLineSegment(sketch, "E13.15.12", {"start": v(8.44, 27.31) * mm, "end": v(8.3, 27.37) * mm});
            skLineSegment(sketch, "E13.15.13", {"start": v(8.15, 27.4) * mm, "end": v(8.3, 27.37) * mm});
            skArc(sketch, "E13.15.14", {"start": v(8.15, 27.4) * mm, "mid": v(8, 27.4) * mm, "end": v(7.86, 27.37) * mm});
            skArc(sketch, "E13.15.15", {"start": v(8.67, 27.12) * mm, "mid": v(8.57, 27.24) * mm, "end": v(8.44, 27.31) * mm});
            skArc(sketch, "E14.trimOffspring", {"start": v(-13.68, 17.52) * mm, "mid": v(-14.1, 17.18) * mm, "end": v(-14.51, 16.83) * mm});
            skArc(sketch, "E15.trimOffspring", {"start": v(-19.34, 10.95) * mm, "mid": v(-19.6, 10.48) * mm, "end": v(-19.85, 10) * mm});
            skArc(sketch, "E16.trimOffspring", {"start": v(-22.06, 2.71) * mm, "mid": v(-22.12, 2.18) * mm, "end": v(-22.16, 1.64) * mm});
            skArc(sketch, "E17.trimOffspring", {"start": v(-21.42, -5.93) * mm, "mid": v(-21.27, -6.45) * mm, "end": v(-21.1, -6.97) * mm});
            skArc(sketch, "E18.trimOffspring", {"start": v(-17.52, -13.68) * mm, "mid": v(-17.18, -14.1) * mm, "end": v(-16.83, -14.51) * mm});
            skArc(sketch, "E19.trimOffspring", {"start": v(-10.95, -19.34) * mm, "mid": v(-10.48, -19.6) * mm, "end": v(-10, -19.85) * mm});
            skArc(sketch, "E20.trimOffspring", {"start": v(-2.71, -22.06) * mm, "mid": v(-2.18, -22.12) * mm, "end": v(-1.64, -22.16) * mm});
            skArc(sketch, "E21.trimOffspring", {"start": v(5.93, -21.42) * mm, "mid": v(6.45, -21.27) * mm, "end": v(6.97, -21.1) * mm});
            skArc(sketch, "E22.trimOffspring", {"start": v(13.68, -17.52) * mm, "mid": v(14.1, -17.18) * mm, "end": v(14.51, -16.83) * mm});
            skArc(sketch, "E23.trimOffspring", {"start": v(19.34, -10.95) * mm, "mid": v(19.6, -10.48) * mm, "end": v(19.85, -10) * mm});
            skArc(sketch, "E24.trimOffspring", {"start": v(22.06, -2.71) * mm, "mid": v(22.12, -2.18) * mm, "end": v(22.16, -1.64) * mm});
            skArc(sketch, "E25.trimOffspring", {"start": v(21.42, 5.93) * mm, "mid": v(21.27, 6.45) * mm, "end": v(21.1, 6.97) * mm});
            skArc(sketch, "E26.trimOffspring", {"start": v(17.52, 13.68) * mm, "mid": v(17.18, 14.1) * mm, "end": v(16.83, 14.51) * mm});
            skArc(sketch, "E27.trimOffspring", {"start": v(10.95, 19.34) * mm, "mid": v(10.48, 19.6) * mm, "end": v(10, 19.85) * mm});
            skArc(sketch, "E28.trimOffspring", {"start": v(2.71, 22.06) * mm, "mid": v(2.18, 22.12) * mm, "end": v(1.64, 22.16) * mm});
            skSolve(sketch);
        }
        {
            var Q0;
            Q0=qCreatedBy(makeId("Front.planeOp"),FACE);
            cPlane(context, id + "F1", {"entities" : qUnion([Q0]), "cplaneType" : CPlaneType.OFFSET, "offset" : 50.8 * mm, "width" : 152.4 * mm, "height" : 152.4 * mm});
        }
        {
            var Q0;
            Q0=qCreatedBy(id+"F1.planeOp",FACE);
            var sketch = newSketch(context, id + "F2", { "sketchPlane" : qUnion([Q0])});
            skArc(sketch, "E29", {"start": v(-5.92, 21.26) * mm, "mid": v(-6.44, 21.1) * mm, "end": v(-6.95, 20.95) * mm});
            skArc(sketch, "E30.trimOffspring", {"start": v(-0.09, 25.49) * mm, "mid": v(-1.02, 27.01) * mm, "end": v(-2.35, 28.22) * mm});
            skLineSegment(sketch, "E31", {"start": v(0.04, 25.01) * mm, "end": v(0.2, 23.43) * mm});
            skLineSegment(sketch, "E32", {"start": v(-2.63, 28.3) * mm, "end": v(-2.79, 28.3) * mm});
            skLineSegment(sketch, "E33.MirrorCS", {"start": v(-2.94, 28.28) * mm, "end": v(-2.79, 28.3) * mm});
            skArc(sketch, "E34.MirrorCS", {"start": v(-4.89, 25.01) * mm, "mid": v(-4.27, 26.7) * mm, "end": v(-3.2, 28.13) * mm});
            skLineSegment(sketch, "E35.MirrorCS", {"start": v(-4.92, 24.52) * mm, "end": v(-4.76, 22.94) * mm});
            skPoint(sketch, "E36.visualSharp", {"position": v(0.33, 22.06) * mm});
            skArc(sketch, "E36.filletArc", {"start": v(0.2, 23.43) * mm, "mid": v(0.66, 22.45) * mm, "end": v(1.66, 22) * mm});
            skPoint(sketch, "E37.visualSharp", {"position": v(-4.63, 21.57) * mm});
            skArc(sketch, "E37.filletArc", {"start": v(-5.92, 21.26) * mm, "mid": v(-5.03, 21.9) * mm, "end": v(-4.76, 22.94) * mm});
            skPoint(sketch, "E38.visualSharp", {"position": v(-4.94, 24.75) * mm});
            skArc(sketch, "E38.filletArc", {"start": v(-4.89, 25.01) * mm, "mid": v(-4.92, 24.77) * mm, "end": v(-4.92, 24.52) * mm});
            skPoint(sketch, "E39.visualSharp", {"position": v(0.02, 25.24) * mm});
            skArc(sketch, "E39.filletArc", {"start": v(0.04, 25.01) * mm, "mid": v(0, 25.25) * mm, "end": v(-0.09, 25.49) * mm});
            skPoint(sketch, "E40.visualSharp", {"position": v(-3.09, 28.25) * mm});
            skArc(sketch, "E40.filletArc", {"start": v(-2.94, 28.28) * mm, "mid": v(-3.08, 28.22) * mm, "end": v(-3.2, 28.13) * mm});
            skPoint(sketch, "E41.visualSharp", {"position": v(-2.48, 28.3) * mm});
            skArc(sketch, "E41.filletArc", {"start": v(-2.35, 28.22) * mm, "mid": v(-2.49, 28.28) * mm, "end": v(-2.63, 28.3) * mm});
            skArc(sketch, "E42.1.0", {"start": v(-13.66, 17.36) * mm, "mid": v(-13.09, 18.28) * mm, "end": v(-13.24, 19.36) * mm});
            skPoint(sketch, "E42.1.1", {"position": v(-14.1, 20.96) * mm});
            skLineSegment(sketch, "E42.1.2", {"start": v(-9.6, 23.1) * mm, "end": v(-8.85, 21.7) * mm});
            skPoint(sketch, "E42.1.3", {"position": v(-9.7, 23.3) * mm});
            skArc(sketch, "E42.1.4", {"start": v(-14.15, 21.22) * mm, "mid": v(-14.22, 23.01) * mm, "end": v(-13.78, 24.75) * mm});
            skLineSegment(sketch, "E42.1.5", {"start": v(-13.99, 20.76) * mm, "end": v(-13.24, 19.36) * mm});
            skArc(sketch, "E42.1.6", {"start": v(-8.85, 21.7) * mm, "mid": v(-8.04, 20.98) * mm, "end": v(-6.95, 20.95) * mm});
            skArc(sketch, "E42.1.7", {"start": v(-9.9, 23.5) * mm, "mid": v(-11.34, 24.55) * mm, "end": v(-13.03, 25.15) * mm});
            skPoint(sketch, "E42.1.8", {"position": v(-13.72, 24.9) * mm});
            skPoint(sketch, "E42.1.9", {"position": v(-13.19, 25.18) * mm});
            skArc(sketch, "E42.1.10", {"start": v(-14.15, 21.22) * mm, "mid": v(-14.09, 20.98) * mm, "end": v(-13.99, 20.76) * mm});
            skArc(sketch, "E42.1.11", {"start": v(-9.6, 23.1) * mm, "mid": v(-9.73, 23.31) * mm, "end": v(-9.9, 23.5) * mm});
            skLineSegment(sketch, "E42.1.12", {"start": v(-13.33, 25.12) * mm, "end": v(-13.47, 25.07) * mm});
            skLineSegment(sketch, "E42.1.13", {"start": v(-13.6, 24.98) * mm, "end": v(-13.47, 25.07) * mm});
            skArc(sketch, "E42.1.14", {"start": v(-13.6, 24.98) * mm, "mid": v(-13.7, 24.88) * mm, "end": v(-13.78, 24.75) * mm});
            skArc(sketch, "E42.1.15", {"start": v(-13.03, 25.15) * mm, "mid": v(-13.18, 25.16) * mm, "end": v(-13.33, 25.12) * mm});
            skArc(sketch, "E42.2.0", {"start": v(-19.32, 10.79) * mm, "mid": v(-19.15, 11.86) * mm, "end": v(-19.7, 12.8) * mm});
            skPoint(sketch, "E42.2.1", {"position": v(-21.1, 13.95) * mm});
            skLineSegment(sketch, "E42.2.2", {"start": v(-17.77, 17.65) * mm, "end": v(-16.54, 16.65) * mm});
            skPoint(sketch, "E42.2.3", {"position": v(-17.94, 17.8) * mm});
            skArc(sketch, "E42.2.4", {"start": v(-21.25, 14.17) * mm, "mid": v(-22, 15.8) * mm, "end": v(-22.27, 17.57) * mm});
            skLineSegment(sketch, "E42.2.5", {"start": v(-20.93, 13.8) * mm, "end": v(-19.7, 12.8) * mm});
            skArc(sketch, "E42.2.6", {"start": v(-16.54, 16.65) * mm, "mid": v(-15.51, 16.29) * mm, "end": v(-14.5, 16.67) * mm});
            skArc(sketch, "E42.2.7", {"start": v(-18.2, 17.9) * mm, "mid": v(-19.93, 18.32) * mm, "end": v(-21.72, 18.23) * mm});
            skPoint(sketch, "E42.2.8", {"position": v(-22.26, 17.73) * mm});
            skPoint(sketch, "E42.2.9", {"position": v(-21.88, 18.2) * mm});
            skArc(sketch, "E42.2.10", {"start": v(-21.25, 14.17) * mm, "mid": v(-21.1, 13.98) * mm, "end": v(-20.93, 13.8) * mm});
            skArc(sketch, "E42.2.11", {"start": v(-17.77, 17.65) * mm, "mid": v(-17.97, 17.8) * mm, "end": v(-18.2, 17.9) * mm});
            skLineSegment(sketch, "E42.2.12", {"start": v(-21.99, 18.1) * mm, "end": v(-22.1, 17.99) * mm});
            skLineSegment(sketch, "E42.2.13", {"start": v(-22.18, 17.86) * mm, "end": v(-22.1, 17.99) * mm});
            skArc(sketch, "E42.2.14", {"start": v(-22.18, 17.86) * mm, "mid": v(-22.24, 17.72) * mm, "end": v(-22.27, 17.57) * mm});
            skArc(sketch, "E42.2.15", {"start": v(-21.72, 18.23) * mm, "mid": v(-21.87, 18.18) * mm, "end": v(-21.99, 18.1) * mm});
            skArc(sketch, "E42.3.0", {"start": v(-22.04, 2.55) * mm, "mid": v(-22.29, 3.61) * mm, "end": v(-23.16, 4.27) * mm});
            skPoint(sketch, "E42.3.1", {"position": v(-24.9, 4.8) * mm});
            skLineSegment(sketch, "E42.3.2", {"start": v(-23.23, 9.5) * mm, "end": v(-21.71, 9.03) * mm});
            skPoint(sketch, "E42.3.3", {"position": v(-23.45, 9.56) * mm});
            skArc(sketch, "E42.3.4", {"start": v(-25.12, 4.94) * mm, "mid": v(-26.43, 6.16) * mm, "end": v(-27.36, 7.7) * mm});
            skLineSegment(sketch, "E42.3.5", {"start": v(-24.68, 4.73) * mm, "end": v(-23.16, 4.27) * mm});
            skArc(sketch, "E42.3.6", {"start": v(-21.71, 9.03) * mm, "mid": v(-20.63, 9.1) * mm, "end": v(-19.83, 9.84) * mm});
            skArc(sketch, "E42.3.7", {"start": v(-23.72, 9.56) * mm, "mid": v(-25.49, 9.28) * mm, "end": v(-27.1, 8.51) * mm});
            skPoint(sketch, "E42.3.8", {"position": v(-27.42, 7.84) * mm});
            skPoint(sketch, "E42.3.9", {"position": v(-27.24, 8.43) * mm});
            skArc(sketch, "E42.3.10", {"start": v(-25.12, 4.94) * mm, "mid": v(-24.9, 4.82) * mm, "end": v(-24.68, 4.73) * mm});
            skArc(sketch, "E42.3.11", {"start": v(-23.23, 9.5) * mm, "mid": v(-23.47, 9.55) * mm, "end": v(-23.72, 9.56) * mm});
            skLineSegment(sketch, "E42.3.12", {"start": v(-27.3, 8.28) * mm, "end": v(-27.36, 8.14) * mm});
            skLineSegment(sketch, "E42.3.13", {"start": v(-27.39, 8) * mm, "end": v(-27.36, 8.14) * mm});
            skArc(sketch, "E42.3.14", {"start": v(-27.39, 8) * mm, "mid": v(-27.4, 7.84) * mm, "end": v(-27.36, 7.7) * mm});
            skArc(sketch, "E42.3.15", {"start": v(-27.1, 8.51) * mm, "mid": v(-27.22, 8.41) * mm, "end": v(-27.3, 8.28) * mm});
            skArc(sketch, "E42.4.0", {"start": v(-21.4, -6.1) * mm, "mid": v(-22.03, -5.2) * mm, "end": v(-23.09, -4.94) * mm});
            skPoint(sketch, "E42.4.1", {"position": v(-24.9, -5.12) * mm});
            skLineSegment(sketch, "E42.4.2", {"start": v(-25.15, -0.14) * mm, "end": v(-23.58, 0.02) * mm});
            skPoint(sketch, "E42.4.3", {"position": v(-25.38, -0.16) * mm});
            skArc(sketch, "E42.4.4", {"start": v(-25.16, -5.06) * mm, "mid": v(-26.84, -4.44) * mm, "end": v(-28.28, -3.38) * mm});
            skLineSegment(sketch, "E42.4.5", {"start": v(-24.67, -5.1) * mm, "end": v(-23.09, -4.94) * mm});
            skArc(sketch, "E42.4.6", {"start": v(-23.58, 0.02) * mm, "mid": v(-22.6, 0.49) * mm, "end": v(-22.15, 1.48) * mm});
            skArc(sketch, "E42.4.7", {"start": v(-25.63, -0.26) * mm, "mid": v(-27.16, -1.2) * mm, "end": v(-28.36, -2.53) * mm});
            skPoint(sketch, "E42.4.8", {"position": v(-28.4, -3.26) * mm});
            skPoint(sketch, "E42.4.9", {"position": v(-28.45, -2.66) * mm});
            skArc(sketch, "E42.4.10", {"start": v(-25.16, -5.06) * mm, "mid": v(-24.91, -5.1) * mm, "end": v(-24.67, -5.1) * mm});
            skArc(sketch, "E42.4.11", {"start": v(-25.15, -0.14) * mm, "mid": v(-25.4, -0.18) * mm, "end": v(-25.63, -0.26) * mm});
            skLineSegment(sketch, "E42.4.12", {"start": v(-28.45, -2.81) * mm, "end": v(-28.45, -2.96) * mm});
            skLineSegment(sketch, "E42.4.13", {"start": v(-28.42, -3.11) * mm, "end": v(-28.45, -2.96) * mm});
            skArc(sketch, "E42.4.14", {"start": v(-28.42, -3.11) * mm, "mid": v(-28.37, -3.26) * mm, "end": v(-28.28, -3.38) * mm});
            skArc(sketch, "E42.4.15", {"start": v(-28.36, -2.53) * mm, "mid": v(-28.43, -2.66) * mm, "end": v(-28.45, -2.81) * mm});
            skArc(sketch, "E42.5.0", {"start": v(-17.5, -13.84) * mm, "mid": v(-18.42, -13.26) * mm, "end": v(-19.5, -13.41) * mm});
            skPoint(sketch, "E42.5.1", {"position": v(-21.1, -14.27) * mm});
            skLineSegment(sketch, "E42.5.2", {"start": v(-23.25, -9.77) * mm, "end": v(-21.85, -9.02) * mm});
            skPoint(sketch, "E42.5.3", {"position": v(-23.45, -9.88) * mm});
            skArc(sketch, "E42.5.4", {"start": v(-21.36, -14.32) * mm, "mid": v(-23.16, -14.4) * mm, "end": v(-24.9, -13.96) * mm});
            skLineSegment(sketch, "E42.5.5", {"start": v(-20.9, -14.16) * mm, "end": v(-19.5, -13.41) * mm});
            skArc(sketch, "E42.5.6", {"start": v(-21.85, -9.02) * mm, "mid": v(-21.12, -8.21) * mm, "end": v(-21.09, -7.13) * mm});
            skArc(sketch, "E42.5.7", {"start": v(-23.64, -10.07) * mm, "mid": v(-24.7, -11.52) * mm, "end": v(-25.3, -13.2) * mm});
            skPoint(sketch, "E42.5.8", {"position": v(-25.04, -13.9) * mm});
            skPoint(sketch, "E42.5.9", {"position": v(-25.33, -13.36) * mm});
            skArc(sketch, "E42.5.10", {"start": v(-21.36, -14.32) * mm, "mid": v(-21.13, -14.26) * mm, "end": v(-20.9, -14.16) * mm});
            skArc(sketch, "E42.5.11", {"start": v(-23.25, -9.77) * mm, "mid": v(-23.46, -9.9) * mm, "end": v(-23.64, -10.07) * mm});
            skLineSegment(sketch, "E42.5.12", {"start": v(-25.27, -13.5) * mm, "end": v(-25.21, -13.64) * mm});
            skLineSegment(sketch, "E42.5.13", {"start": v(-25.13, -13.77) * mm, "end": v(-25.21, -13.64) * mm});
            skArc(sketch, "E42.5.14", {"start": v(-25.13, -13.77) * mm, "mid": v(-25.02, -13.88) * mm, "end": v(-24.9, -13.96) * mm});
            skArc(sketch, "E42.5.15", {"start": v(-25.3, -13.2) * mm, "mid": v(-25.3, -13.36) * mm, "end": v(-25.27, -13.5) * mm});
            skArc(sketch, "E42.6.0", {"start": v(-10.93, -19.5) * mm, "mid": v(-12, -19.32) * mm, "end": v(-12.94, -19.87) * mm});
            skPoint(sketch, "E42.6.1", {"position": v(-14.1, -21.28) * mm});
            skLineSegment(sketch, "E42.6.2", {"start": v(-17.8, -17.94) * mm, "end": v(-16.8, -16.72) * mm});
            skPoint(sketch, "E42.6.3", {"position": v(-17.94, -18.12) * mm});
            skArc(sketch, "E42.6.4", {"start": v(-14.32, -21.43) * mm, "mid": v(-15.94, -22.18) * mm, "end": v(-17.72, -22.44) * mm});
            skLineSegment(sketch, "E42.6.5", {"start": v(-13.95, -21.1) * mm, "end": v(-12.94, -19.87) * mm});
            skArc(sketch, "E42.6.6", {"start": v(-16.8, -16.72) * mm, "mid": v(-16.43, -15.69) * mm, "end": v(-16.82, -14.67) * mm});
            skArc(sketch, "E42.6.7", {"start": v(-18.05, -18.37) * mm, "mid": v(-18.46, -20.1) * mm, "end": v(-18.38, -21.9) * mm});
            skPoint(sketch, "E42.6.8", {"position": v(-17.88, -22.44) * mm});
            skPoint(sketch, "E42.6.9", {"position": v(-18.35, -22.05) * mm});
            skArc(sketch, "E42.6.10", {"start": v(-14.32, -21.43) * mm, "mid": v(-14.12, -21.28) * mm, "end": v(-13.95, -21.1) * mm});
            skArc(sketch, "E42.6.11", {"start": v(-17.8, -17.94) * mm, "mid": v(-17.94, -18.14) * mm, "end": v(-18.05, -18.37) * mm});
            skLineSegment(sketch, "E42.6.12", {"start": v(-18.24, -22.16) * mm, "end": v(-18.13, -22.27) * mm});
            skLineSegment(sketch, "E42.6.13", {"start": v(-18, -22.36) * mm, "end": v(-18.13, -22.27) * mm});
            skArc(sketch, "E42.6.14", {"start": v(-18, -22.36) * mm, "mid": v(-17.87, -22.42) * mm, "end": v(-17.72, -22.44) * mm});
            skArc(sketch, "E42.6.15", {"start": v(-18.38, -21.9) * mm, "mid": v(-18.33, -22.04) * mm, "end": v(-18.24, -22.16) * mm});
            skArc(sketch, "E42.7.0", {"start": v(-2.7, -22.22) * mm, "mid": v(-3.76, -22.46) * mm, "end": v(-4.41, -23.33) * mm});
            skPoint(sketch, "E42.7.1", {"position": v(-4.94, -25.07) * mm});
            skLineSegment(sketch, "E42.7.2", {"start": v(-9.64, -23.4) * mm, "end": v(-9.18, -21.89) * mm});
            skPoint(sketch, "E42.7.3", {"position": v(-9.7, -23.63) * mm});
            skArc(sketch, "E42.7.4", {"start": v(-5.09, -25.3) * mm, "mid": v(-6.3, -26.6) * mm, "end": v(-7.84, -27.53) * mm});
            skLineSegment(sketch, "E42.7.5", {"start": v(-4.87, -24.85) * mm, "end": v(-4.41, -23.33) * mm});
            skArc(sketch, "E42.7.6", {"start": v(-9.18, -21.89) * mm, "mid": v(-9.24, -20.8) * mm, "end": v(-9.98, -20) * mm});
            skArc(sketch, "E42.7.7", {"start": v(-9.7, -23.9) * mm, "mid": v(-9.42, -25.66) * mm, "end": v(-8.66, -27.28) * mm});
            skPoint(sketch, "E42.7.8", {"position": v(-7.99, -27.6) * mm});
            skPoint(sketch, "E42.7.9", {"position": v(-8.57, -27.41) * mm});
            skArc(sketch, "E42.7.10", {"start": v(-5.09, -25.3) * mm, "mid": v(-4.96, -25.08) * mm, "end": v(-4.87, -24.85) * mm});
            skArc(sketch, "E42.7.11", {"start": v(-9.64, -23.4) * mm, "mid": v(-9.7, -23.65) * mm, "end": v(-9.7, -23.9) * mm});
            skLineSegment(sketch, "E42.7.12", {"start": v(-8.43, -27.47) * mm, "end": v(-8.29, -27.53) * mm});
            skLineSegment(sketch, "E42.7.13", {"start": v(-8.14, -27.56) * mm, "end": v(-8.29, -27.53) * mm});
            skArc(sketch, "E42.7.14", {"start": v(-8.14, -27.56) * mm, "mid": v(-7.99, -27.57) * mm, "end": v(-7.84, -27.53) * mm});
            skArc(sketch, "E42.7.15", {"start": v(-8.66, -27.28) * mm, "mid": v(-8.56, -27.4) * mm, "end": v(-8.43, -27.47) * mm});
            skArc(sketch, "E42.8.0", {"start": v(5.95, -21.58) * mm, "mid": v(5.06, -22.21) * mm, "end": v(4.8, -23.26) * mm});
            skPoint(sketch, "E42.8.1", {"position": v(4.97, -25.07) * mm});
            skLineSegment(sketch, "E42.8.2", {"start": v(0, -25.33) * mm, "end": v(-0.16, -23.75) * mm});
            skPoint(sketch, "E42.8.3", {"position": v(0.02, -25.56) * mm});
            skArc(sketch, "E42.8.4", {"start": v(4.92, -25.33) * mm, "mid": v(4.3, -27.01) * mm, "end": v(3.23, -28.45) * mm});
            skLineSegment(sketch, "E42.8.5", {"start": v(4.95, -24.84) * mm, "end": v(4.8, -23.26) * mm});
            skArc(sketch, "E42.8.6", {"start": v(-0.16, -23.75) * mm, "mid": v(-0.63, -22.77) * mm, "end": v(-1.62, -22.32) * mm});
            skArc(sketch, "E42.8.7", {"start": v(0.12, -25.8) * mm, "mid": v(1.05, -27.33) * mm, "end": v(2.38, -28.54) * mm});
            skPoint(sketch, "E42.8.8", {"position": v(3.12, -28.57) * mm});
            skPoint(sketch, "E42.8.9", {"position": v(2.51, -28.63) * mm});
            skArc(sketch, "E42.8.10", {"start": v(4.92, -25.33) * mm, "mid": v(4.95, -25.09) * mm, "end": v(4.95, -24.84) * mm});
            skArc(sketch, "E42.8.11", {"start": v(0, -25.33) * mm, "mid": v(0.04, -25.57) * mm, "end": v(0.12, -25.8) * mm});
            skLineSegment(sketch, "E42.8.12", {"start": v(2.67, -28.63) * mm, "end": v(2.82, -28.63) * mm});
            skLineSegment(sketch, "E42.8.13", {"start": v(2.97, -28.6) * mm, "end": v(2.82, -28.63) * mm});
            skArc(sketch, "E42.8.14", {"start": v(2.97, -28.6) * mm, "mid": v(3.11, -28.54) * mm, "end": v(3.23, -28.45) * mm});
            skArc(sketch, "E42.8.15", {"start": v(2.38, -28.54) * mm, "mid": v(2.52, -28.6) * mm, "end": v(2.67, -28.63) * mm});
            skArc(sketch, "E42.9.0", {"start": v(13.7, -17.68) * mm, "mid": v(13.12, -18.6) * mm, "end": v(13.27, -19.68) * mm});
            skPoint(sketch, "E42.9.1", {"position": v(14.13, -21.28) * mm});
            skLineSegment(sketch, "E42.9.2", {"start": v(9.63, -23.42) * mm, "end": v(8.88, -22.02) * mm});
            skPoint(sketch, "E42.9.3", {"position": v(9.74, -23.63) * mm});
            skArc(sketch, "E42.9.4", {"start": v(14.18, -21.54) * mm, "mid": v(14.25, -23.33) * mm, "end": v(13.81, -25.07) * mm});
            skLineSegment(sketch, "E42.9.5", {"start": v(14.02, -21.08) * mm, "end": v(13.27, -19.68) * mm});
            skArc(sketch, "E42.9.6", {"start": v(8.88, -22.02) * mm, "mid": v(8.07, -21.3) * mm, "end": v(6.98, -21.26) * mm});
            skArc(sketch, "E42.9.7", {"start": v(9.92, -23.82) * mm, "mid": v(11.37, -24.87) * mm, "end": v(13.06, -25.47) * mm});
            skPoint(sketch, "E42.9.8", {"position": v(13.75, -25.22) * mm});
            skPoint(sketch, "E42.9.9", {"position": v(13.22, -25.5) * mm});
            skArc(sketch, "E42.9.10", {"start": v(14.18, -21.54) * mm, "mid": v(14.12, -21.3) * mm, "end": v(14.02, -21.08) * mm});
            skArc(sketch, "E42.9.11", {"start": v(9.63, -23.42) * mm, "mid": v(9.76, -23.63) * mm, "end": v(9.92, -23.82) * mm});
            skLineSegment(sketch, "E42.9.12", {"start": v(13.36, -25.44) * mm, "end": v(13.5, -25.39) * mm});
            skLineSegment(sketch, "E42.9.13", {"start": v(13.63, -25.3) * mm, "end": v(13.5, -25.39) * mm});
            skArc(sketch, "E42.9.14", {"start": v(13.63, -25.3) * mm, "mid": v(13.74, -25.2) * mm, "end": v(13.81, -25.07) * mm});
            skArc(sketch, "E42.9.15", {"start": v(13.06, -25.47) * mm, "mid": v(13.21, -25.48) * mm, "end": v(13.36, -25.44) * mm});
            skArc(sketch, "E42.10.0", {"start": v(19.36, -11.1) * mm, "mid": v(19.18, -12.18) * mm, "end": v(19.73, -13.12) * mm});
            skPoint(sketch, "E42.10.1", {"position": v(21.14, -14.27) * mm});
            skLineSegment(sketch, "E42.10.2", {"start": v(17.8, -17.97) * mm, "end": v(16.57, -16.97) * mm});
            skPoint(sketch, "E42.10.3", {"position": v(17.98, -18.12) * mm});
            skArc(sketch, "E42.10.4", {"start": v(21.28, -14.5) * mm, "mid": v(22.03, -16.12) * mm, "end": v(22.3, -17.9) * mm});
            skLineSegment(sketch, "E42.10.5", {"start": v(20.96, -14.13) * mm, "end": v(19.73, -13.12) * mm});
            skArc(sketch, "E42.10.6", {"start": v(16.57, -16.97) * mm, "mid": v(15.55, -16.6) * mm, "end": v(14.53, -17) * mm});
            skArc(sketch, "E42.10.7", {"start": v(18.22, -18.22) * mm, "mid": v(19.96, -18.64) * mm, "end": v(21.76, -18.55) * mm});
            skPoint(sketch, "E42.10.8", {"position": v(22.3, -18.05) * mm});
            skPoint(sketch, "E42.10.9", {"position": v(21.91, -18.52) * mm});
            skArc(sketch, "E42.10.10", {"start": v(21.28, -14.5) * mm, "mid": v(21.13, -14.3) * mm, "end": v(20.96, -14.13) * mm});
            skArc(sketch, "E42.10.11", {"start": v(17.8, -17.97) * mm, "mid": v(18, -18.12) * mm, "end": v(18.22, -18.22) * mm});
            skLineSegment(sketch, "E42.10.12", {"start": v(22.02, -18.41) * mm, "end": v(22.13, -18.3) * mm});
            skLineSegment(sketch, "E42.10.13", {"start": v(22.21, -18.18) * mm, "end": v(22.13, -18.3) * mm});
            skArc(sketch, "E42.10.14", {"start": v(22.21, -18.18) * mm, "mid": v(22.28, -18.04) * mm, "end": v(22.3, -17.9) * mm});
            skArc(sketch, "E42.10.15", {"start": v(21.76, -18.55) * mm, "mid": v(21.9, -18.5) * mm, "end": v(22.02, -18.41) * mm});
            skArc(sketch, "E42.11.0", {"start": v(22.07, -2.87) * mm, "mid": v(22.32, -3.93) * mm, "end": v(23.19, -4.59) * mm});
            skPoint(sketch, "E42.11.1", {"position": v(24.93, -5.12) * mm});
            skLineSegment(sketch, "E42.11.2", {"start": v(23.26, -9.81) * mm, "end": v(21.74, -9.35) * mm});
            skPoint(sketch, "E42.11.3", {"position": v(23.48, -9.88) * mm});
            skArc(sketch, "E42.11.4", {"start": v(25.15, -5.26) * mm, "mid": v(26.46, -6.48) * mm, "end": v(27.39, -8.02) * mm});
            skLineSegment(sketch, "E42.11.5", {"start": v(24.7, -5.05) * mm, "end": v(23.19, -4.59) * mm});
            skArc(sketch, "E42.11.6", {"start": v(21.74, -9.35) * mm, "mid": v(20.66, -9.41) * mm, "end": v(19.87, -10.16) * mm});
            skArc(sketch, "E42.11.7", {"start": v(23.75, -9.88) * mm, "mid": v(25.52, -9.6) * mm, "end": v(27.14, -8.83) * mm});
            skPoint(sketch, "E42.11.8", {"position": v(27.45, -8.16) * mm});
            skPoint(sketch, "E42.11.9", {"position": v(27.27, -8.74) * mm});
            skArc(sketch, "E42.11.10", {"start": v(25.15, -5.26) * mm, "mid": v(24.94, -5.14) * mm, "end": v(24.7, -5.05) * mm});
            skArc(sketch, "E42.11.11", {"start": v(23.26, -9.81) * mm, "mid": v(23.5, -9.87) * mm, "end": v(23.75, -9.88) * mm});
            skLineSegment(sketch, "E42.11.12", {"start": v(27.33, -8.6) * mm, "end": v(27.39, -8.46) * mm});
            skLineSegment(sketch, "E42.11.13", {"start": v(27.42, -8.31) * mm, "end": v(27.39, -8.46) * mm});
            skArc(sketch, "E42.11.14", {"start": v(27.42, -8.31) * mm, "mid": v(27.42, -8.16) * mm, "end": v(27.39, -8.02) * mm});
            skArc(sketch, "E42.11.15", {"start": v(27.14, -8.83) * mm, "mid": v(27.25, -8.73) * mm, "end": v(27.33, -8.6) * mm});
            skArc(sketch, "E42.12.0", {"start": v(21.43, 5.77) * mm, "mid": v(22.07, 4.89) * mm, "end": v(23.12, 4.62) * mm});
            skPoint(sketch, "E42.12.1", {"position": v(24.93, 4.8) * mm});
            skLineSegment(sketch, "E42.12.2", {"start": v(25.19, -0.18) * mm, "end": v(23.6, -0.34) * mm});
            skPoint(sketch, "E42.12.3", {"position": v(25.42, -0.16) * mm});
            skArc(sketch, "E42.12.4", {"start": v(25.19, 4.74) * mm, "mid": v(26.87, 4.12) * mm, "end": v(28.31, 3.06) * mm});
            skLineSegment(sketch, "E42.12.5", {"start": v(24.7, 4.77) * mm, "end": v(23.12, 4.62) * mm});
            skArc(sketch, "E42.12.6", {"start": v(23.6, -0.34) * mm, "mid": v(22.63, -0.8) * mm, "end": v(22.18, -1.8) * mm});
            skArc(sketch, "E42.12.7", {"start": v(25.66, -0.06) * mm, "mid": v(27.19, 0.88) * mm, "end": v(28.4, 2.2) * mm});
            skPoint(sketch, "E42.12.8", {"position": v(28.42, 2.94) * mm});
            skPoint(sketch, "E42.12.9", {"position": v(28.48, 2.34) * mm});
            skArc(sketch, "E42.12.10", {"start": v(25.19, 4.74) * mm, "mid": v(24.94, 4.78) * mm, "end": v(24.7, 4.77) * mm});
            skArc(sketch, "E42.12.11", {"start": v(25.19, -0.18) * mm, "mid": v(25.43, -0.14) * mm, "end": v(25.66, -0.06) * mm});
            skLineSegment(sketch, "E42.12.12", {"start": v(28.48, 2.5) * mm, "end": v(28.48, 2.64) * mm});
            skLineSegment(sketch, "E42.12.13", {"start": v(28.45, 2.8) * mm, "end": v(28.48, 2.64) * mm});
            skArc(sketch, "E42.12.14", {"start": v(28.45, 2.8) * mm, "mid": v(28.4, 2.94) * mm, "end": v(28.31, 3.06) * mm});
            skArc(sketch, "E42.12.15", {"start": v(28.4, 2.2) * mm, "mid": v(28.46, 2.34) * mm, "end": v(28.48, 2.5) * mm});
            skArc(sketch, "E42.13.0", {"start": v(17.53, 13.52) * mm, "mid": v(18.46, 12.94) * mm, "end": v(19.53, 13.1) * mm});
            skPoint(sketch, "E42.13.1", {"position": v(21.14, 13.95) * mm});
            skLineSegment(sketch, "E42.13.2", {"start": v(23.28, 9.45) * mm, "end": v(21.88, 8.7) * mm});
            skPoint(sketch, "E42.13.3", {"position": v(23.48, 9.56) * mm});
            skArc(sketch, "E42.13.4", {"start": v(21.4, 14) * mm, "mid": v(23.19, 14.07) * mm, "end": v(24.93, 13.64) * mm});
            skLineSegment(sketch, "E42.13.5", {"start": v(20.93, 13.84) * mm, "end": v(19.53, 13.1) * mm});
            skArc(sketch, "E42.13.6", {"start": v(21.88, 8.7) * mm, "mid": v(21.15, 7.9) * mm, "end": v(21.12, 6.8) * mm});
            skArc(sketch, "E42.13.7", {"start": v(23.67, 9.75) * mm, "mid": v(24.72, 11.2) * mm, "end": v(25.33, 12.89) * mm});
            skPoint(sketch, "E42.13.8", {"position": v(25.07, 13.58) * mm});
            skPoint(sketch, "E42.13.9", {"position": v(25.36, 13.04) * mm});
            skArc(sketch, "E42.13.10", {"start": v(21.4, 14) * mm, "mid": v(21.16, 13.94) * mm, "end": v(20.93, 13.84) * mm});
            skArc(sketch, "E42.13.11", {"start": v(23.28, 9.45) * mm, "mid": v(23.49, 9.58) * mm, "end": v(23.67, 9.75) * mm});
            skLineSegment(sketch, "E42.13.12", {"start": v(25.3, 13.18) * mm, "end": v(25.24, 13.32) * mm});
            skLineSegment(sketch, "E42.13.13", {"start": v(25.16, 13.45) * mm, "end": v(25.24, 13.32) * mm});
            skArc(sketch, "E42.13.14", {"start": v(25.16, 13.45) * mm, "mid": v(25.06, 13.56) * mm, "end": v(24.93, 13.64) * mm});
            skArc(sketch, "E42.13.15", {"start": v(25.33, 12.89) * mm, "mid": v(25.34, 13.04) * mm, "end": v(25.3, 13.18) * mm});
            skArc(sketch, "E42.14.0", {"start": v(10.97, 19.18) * mm, "mid": v(12.04, 19) * mm, "end": v(12.97, 19.56) * mm});
            skPoint(sketch, "E42.14.1", {"position": v(14.13, 20.96) * mm});
            skLineSegment(sketch, "E42.14.2", {"start": v(17.83, 17.62) * mm, "end": v(16.82, 16.4) * mm});
            skPoint(sketch, "E42.14.3", {"position": v(17.98, 17.8) * mm});
            skArc(sketch, "E42.14.4", {"start": v(14.35, 21.1) * mm, "mid": v(15.98, 21.86) * mm, "end": v(17.75, 22.12) * mm});
            skLineSegment(sketch, "E42.14.5", {"start": v(13.98, 20.78) * mm, "end": v(12.97, 19.56) * mm});
            skArc(sketch, "E42.14.6", {"start": v(16.82, 16.4) * mm, "mid": v(16.46, 15.37) * mm, "end": v(16.85, 14.35) * mm});
            skArc(sketch, "E42.14.7", {"start": v(18.08, 18.05) * mm, "mid": v(18.5, 19.79) * mm, "end": v(18.4, 21.58) * mm});
            skPoint(sketch, "E42.14.8", {"position": v(17.9, 22.12) * mm});
            skPoint(sketch, "E42.14.9", {"position": v(18.38, 21.73) * mm});
            skArc(sketch, "E42.14.10", {"start": v(14.35, 21.1) * mm, "mid": v(14.15, 20.96) * mm, "end": v(13.98, 20.78) * mm});
            skArc(sketch, "E42.14.11", {"start": v(17.83, 17.62) * mm, "mid": v(17.97, 17.82) * mm, "end": v(18.08, 18.05) * mm});
            skLineSegment(sketch, "E42.14.12", {"start": v(18.27, 21.84) * mm, "end": v(18.16, 21.95) * mm});
            skLineSegment(sketch, "E42.14.13", {"start": v(18.03, 22.04) * mm, "end": v(18.16, 21.95) * mm});
            skArc(sketch, "E42.14.14", {"start": v(18.03, 22.04) * mm, "mid": v(17.9, 22.1) * mm, "end": v(17.75, 22.12) * mm});
            skArc(sketch, "E42.14.15", {"start": v(18.4, 21.58) * mm, "mid": v(18.36, 21.72) * mm, "end": v(18.27, 21.84) * mm});
            skArc(sketch, "E42.15.0", {"start": v(2.73, 21.9) * mm, "mid": v(3.8, 22.14) * mm, "end": v(4.44, 23.01) * mm});
            skPoint(sketch, "E42.15.1", {"position": v(4.97, 24.75) * mm});
            skLineSegment(sketch, "E42.15.2", {"start": v(9.67, 23.09) * mm, "end": v(9.2, 21.57) * mm});
            skPoint(sketch, "E42.15.3", {"position": v(9.74, 23.3) * mm});
            skArc(sketch, "E42.15.4", {"start": v(5.12, 24.97) * mm, "mid": v(6.34, 26.29) * mm, "end": v(7.87, 27.21) * mm});
            skLineSegment(sketch, "E42.15.5", {"start": v(4.9, 24.53) * mm, "end": v(4.44, 23.01) * mm});
            skArc(sketch, "E42.15.6", {"start": v(9.2, 21.57) * mm, "mid": v(9.27, 20.48) * mm, "end": v(10.01, 19.69) * mm});
            skArc(sketch, "E42.15.7", {"start": v(9.74, 23.57) * mm, "mid": v(9.46, 25.34) * mm, "end": v(8.69, 26.96) * mm});
            skPoint(sketch, "E42.15.8", {"position": v(8.02, 27.27) * mm});
            skPoint(sketch, "E42.15.9", {"position": v(8.6, 27.1) * mm});
            skArc(sketch, "E42.15.10", {"start": v(5.12, 24.97) * mm, "mid": v(5, 24.76) * mm, "end": v(4.9, 24.53) * mm});
            skArc(sketch, "E42.15.11", {"start": v(9.67, 23.09) * mm, "mid": v(9.72, 23.33) * mm, "end": v(9.74, 23.57) * mm});
            skLineSegment(sketch, "E42.15.12", {"start": v(8.46, 27.15) * mm, "end": v(8.32, 27.21) * mm});
            skLineSegment(sketch, "E42.15.13", {"start": v(8.17, 27.24) * mm, "end": v(8.32, 27.21) * mm});
            skArc(sketch, "E42.15.14", {"start": v(8.17, 27.24) * mm, "mid": v(8.02, 27.25) * mm, "end": v(7.87, 27.21) * mm});
            skArc(sketch, "E42.15.15", {"start": v(8.69, 26.96) * mm, "mid": v(8.59, 27.08) * mm, "end": v(8.46, 27.15) * mm});
            skArc(sketch, "E43.trimOffspring", {"start": v(-13.66, 17.36) * mm, "mid": v(-14.08, 17.02) * mm, "end": v(-14.5, 16.67) * mm});
            skArc(sketch, "E44.trimOffspring", {"start": v(-19.32, 10.79) * mm, "mid": v(-19.58, 10.32) * mm, "end": v(-19.83, 9.84) * mm});
            skArc(sketch, "E45.trimOffspring", {"start": v(-22.04, 2.55) * mm, "mid": v(-22.1, 2.02) * mm, "end": v(-22.15, 1.48) * mm});
            skArc(sketch, "E46.trimOffspring", {"start": v(-21.4, -6.1) * mm, "mid": v(-21.25, -6.61) * mm, "end": v(-21.09, -7.13) * mm});
            skArc(sketch, "E47.trimOffspring", {"start": v(-17.5, -13.84) * mm, "mid": v(-17.16, -14.26) * mm, "end": v(-16.82, -14.67) * mm});
            skArc(sketch, "E48.trimOffspring", {"start": v(-10.93, -19.5) * mm, "mid": v(-10.46, -19.76) * mm, "end": v(-9.98, -20) * mm});
            skArc(sketch, "E49.trimOffspring", {"start": v(-2.7, -22.22) * mm, "mid": v(-2.16, -22.28) * mm, "end": v(-1.62, -22.32) * mm});
            skArc(sketch, "E50.trimOffspring", {"start": v(5.95, -21.58) * mm, "mid": v(6.47, -21.43) * mm, "end": v(6.98, -21.26) * mm});
            skArc(sketch, "E51.trimOffspring", {"start": v(13.7, -17.68) * mm, "mid": v(14.12, -17.34) * mm, "end": v(14.53, -17) * mm});
            skArc(sketch, "E52.trimOffspring", {"start": v(19.36, -11.1) * mm, "mid": v(19.62, -10.64) * mm, "end": v(19.87, -10.16) * mm});
            skArc(sketch, "E53.trimOffspring", {"start": v(22.07, -2.87) * mm, "mid": v(22.13, -2.34) * mm, "end": v(22.18, -1.8) * mm});
            skArc(sketch, "E54.trimOffspring", {"start": v(21.43, 5.77) * mm, "mid": v(21.28, 6.3) * mm, "end": v(21.12, 6.8) * mm});
            skArc(sketch, "E55.trimOffspring", {"start": v(17.53, 13.52) * mm, "mid": v(17.2, 13.94) * mm, "end": v(16.85, 14.35) * mm});
            skArc(sketch, "E56.trimOffspring", {"start": v(10.97, 19.18) * mm, "mid": v(10.5, 19.44) * mm, "end": v(10.01, 19.69) * mm});
            skArc(sketch, "E57.trimOffspring", {"start": v(2.73, 21.9) * mm, "mid": v(2.2, 21.96) * mm, "end": v(1.66, 22) * mm});
            skSolve(sketch);
        }
        {
            var Q0;
            Q0=makeQuery(id+"F2.imprint","IMPRINT",FACE,{"disambiguationData":[TD([[makeQuery(id+"F2.imprint","IMPRINT",EDGE,{"derivedFrom":sQuery(id+"F2.wireOp",EDGE,"E29")}),1.0]])]});
            var Q1;
            Q1=makeQuery(id+"F0.imprint","IMPRINT",FACE,{"disambiguationData":[TD([[makeQuery(id+"F0.imprint","IMPRINT",EDGE,{"derivedFrom":sQuery(id+"F0.wireOp",EDGE,"E0")}),1.0]])]});
            var Q2;
            Q2=sQuery(id+"F2.wireOp",VERTEX,"E33.MirrorCS.end");
            var Q3;
            Q3=sQuery(id+"F0.wireOp",VERTEX,"E13.1.12.end");
            loft(context, id + "F3", {"sheetProfilesArray" : [{ "sheetProfileEntities" : qUnion([Q0]) }, { "sheetProfileEntities" : qUnion([Q1]) }], "matchConnections" : true, "connections" : [{ "connectionEntities" : qUnion([Q2, Q3]), "connectionEdgeQueries" : qUnion([]), "connectionEdgeParameters" : [] }]});
        }
        {
            var Q0;
            Q0=sQuery(id+"F2.wireOp",VERTEX,"E29.center");
            var Q1;
            Q1=makeQuery(id+"F3.opLoft","SWEPT_BODY",BODY,{"disambiguationData":[OSD([makeQuery(id+"F0.imprint","IMPRINT",FACE,{"disambiguationData":[TD([[makeQuery(id+"F0.imprint","IMPRINT",EDGE,{"derivedFrom":sQuery(id+"F0.wireOp",EDGE,"E0")}),1.0]])]}),makeQuery(id+"F2.imprint","IMPRINT",FACE,{"disambiguationData":[TD([[makeQuery(id+"F2.imprint","IMPRINT",EDGE,{"derivedFrom":sQuery(id+"F2.wireOp",EDGE,"E29")}),1.0]])]})])]});
            hole(context, id + "F4", {"style" : HoleStyle.SIMPLE, "endStyle" : HoleEndStyle.BLIND, "holeDiameter" : 12.7 * mm, "holeDepth" : 50.8 * mm, "tappedDepth" : 12.7 * mm, "tapClearance" : 3, "locations" : qUnion([Q0]), "scope" : qUnion([Q1])});
        }
    });
